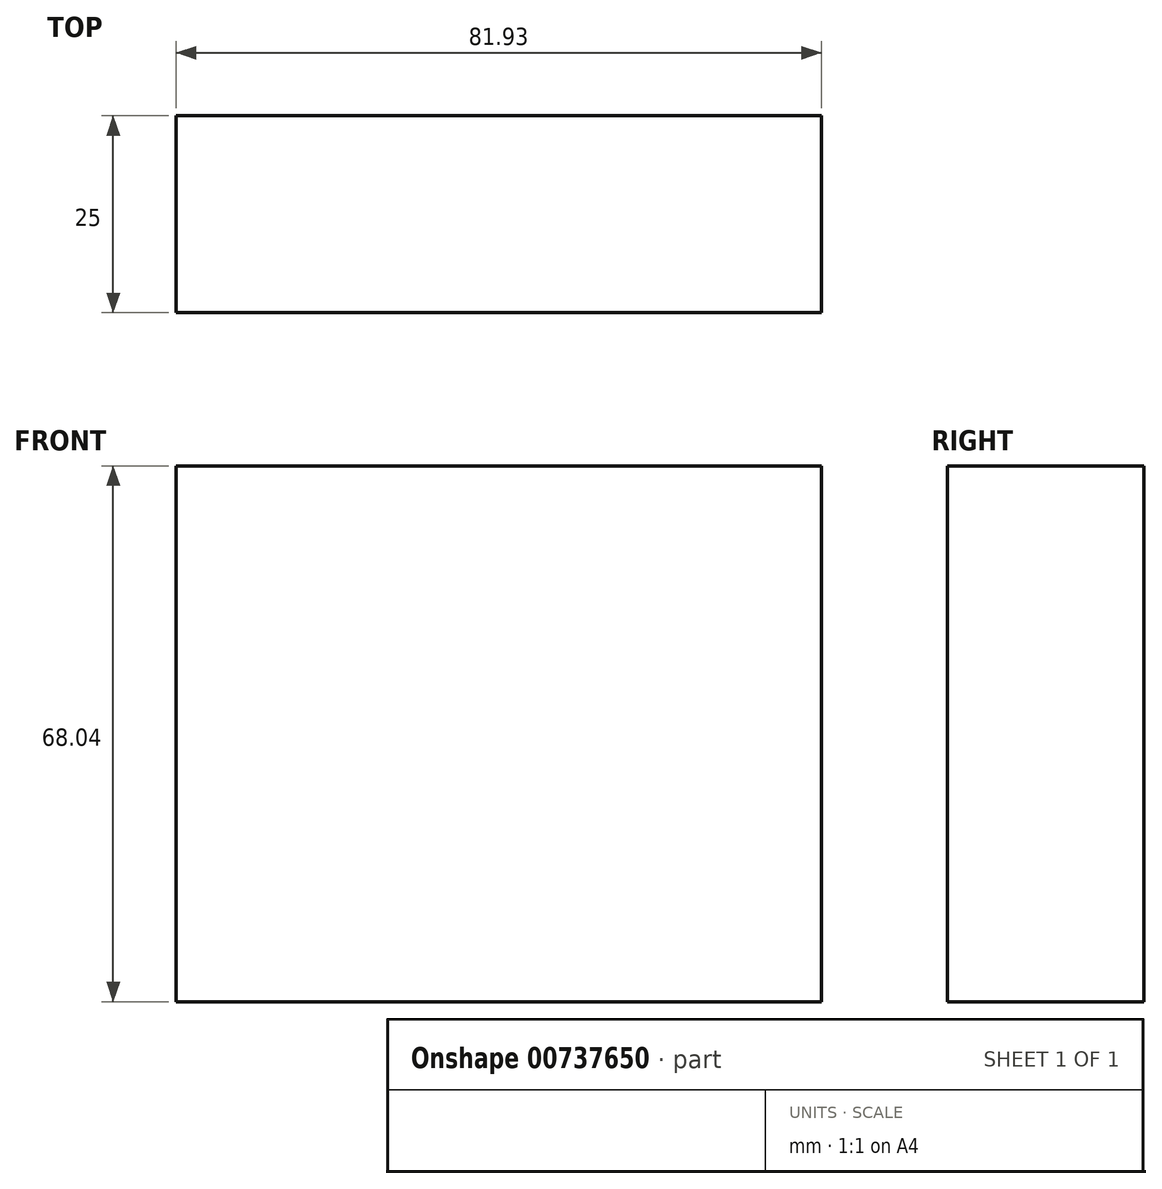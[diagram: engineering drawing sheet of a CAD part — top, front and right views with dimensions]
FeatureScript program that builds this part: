
annotation { "Feature Type Name" : "Feature", "Feature Type Description" : "" }
export const myFeature = defineFeature(function(context is Context, id is Id, definition is map)
    precondition{}
    {
        {
            var Q0;
            Q0=qCreatedBy(makeId("Front.planeOp"),FACE);
            var sketch = newSketch(context, id + "F0", { "sketchPlane" : qUnion([Q0])});
            skLineSegment(sketch, "E0.bottom", {"start": v(22.2, 33.23) * mm, "end": v(104.13, 33.23) * mm});
            skLineSegment(sketch, "E0.top", {"start": v(22.2, 101.27) * mm, "end": v(104.13, 101.27) * mm});
            skLineSegment(sketch, "E0.left", {"start": v(22.2, 33.23) * mm, "end": v(22.2, 101.27) * mm});
            skLineSegment(sketch, "E0.right", {"start": v(104.13, 33.23) * mm, "end": v(104.13, 101.27) * mm});
            skSolve(sketch);
        }
        {
            var Q0;
            Q0=makeQuery(id+"F0.imprint","IMPRINT",FACE,{"disambiguationData":[TD([[makeQuery(id+"F0.imprint","IMPRINT",EDGE,{"derivedFrom":sQuery(id+"F0.wireOp",EDGE,"E0.bottom")}),1.0]])]});
            extrude(context, id + "F1", {"entities" : qUnion([Q0]), "depth" : 25 * mm, "offsetDistance" : 25 * mm});
        }
    });
